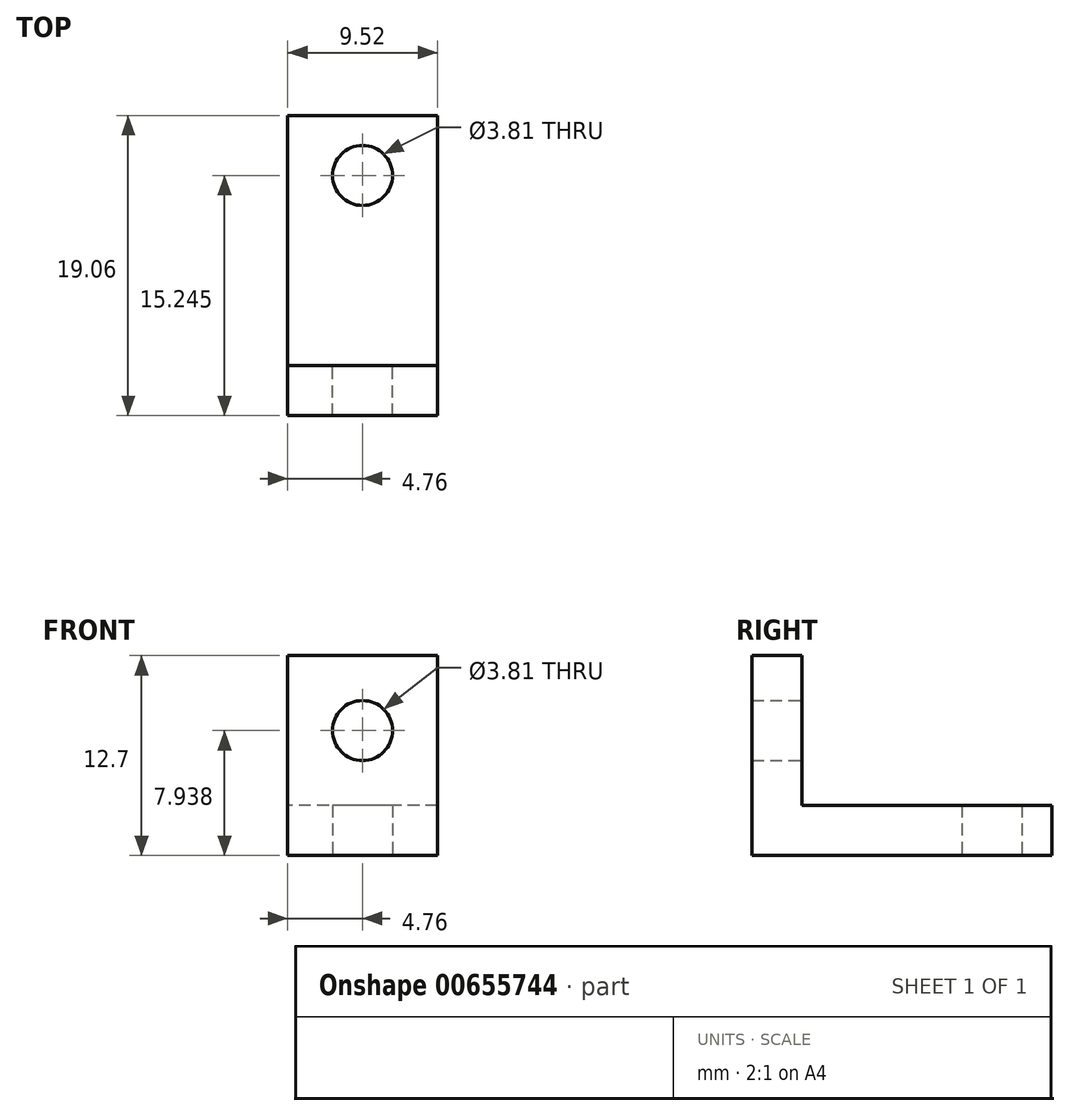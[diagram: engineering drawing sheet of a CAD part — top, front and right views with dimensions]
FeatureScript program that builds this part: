
annotation { "Feature Type Name" : "Feature", "Feature Type Description" : "" }
export const myFeature = defineFeature(function(context is Context, id is Id, definition is map)
    precondition{}
    {
        {
            var Q0;
            Q0=qCreatedBy(makeId("Top.planeOp"),FACE);
            var sketch = newSketch(context, id + "F0", { "sketchPlane" : qUnion([Q0])});
            skLineSegment(sketch, "E0.bottom", {"start": v(4.76, -9.53) * mm, "end": v(-4.76, -9.53) * mm});
            skLineSegment(sketch, "E0.top", {"start": v(4.76, 9.53) * mm, "end": v(-4.76, 9.52) * mm});
            skLineSegment(sketch, "E0.left", {"start": v(4.76, -9.52) * mm, "end": v(4.76, 9.53) * mm});
            skLineSegment(sketch, "E0.right", {"start": v(-4.76, -9.53) * mm, "end": v(-4.76, 9.52) * mm});
            skPoint(sketch, "E0.middle", {"position": v(0, 0) * mm});
            skLineSegment(sketch, "E1", {"start": v(-4.76, -6.35) * mm, "end": v(4.76, -6.35) * mm});
            skCircle(sketch, "E2", {"center": v(0, 5.72) * mm, "radius": 1.9 * mm});
            skPoint(sketch, "E2.centerSnap0", {"position": v(0, 9.53) * mm});
            skSolve(sketch);
        }
        {
            var Q0;
            {var subQ1=sQuery(id+"F0.wireOp",EDGE,"E0.top");Q0=makeQuery(id+"F0.imprint","IMPRINT",FACE,{"disambiguationData":[TD([[makeQuery(id+"F0.imprint","IMPRINT",EDGE,{"derivedFrom":subQ1}),1.0]])]});}
            extrude(context, id + "F1", {"entities" : qUnion([Q0]), "depth" : 3.17 * mm, "offsetDistance" : 25.4 * mm});
        }
        {
            var Q0;
            {var subQ0=sQuery(id+"F0.wireOp",EDGE,"E0.bottom");Q0=makeQuery(id+"F0.imprint","IMPRINT",FACE,{"disambiguationData":[TD([[makeQuery(id+"F0.imprint","IMPRINT",EDGE,{"derivedFrom":subQ0}),-1.0]])]});}
            extrude(context, id + "F2", {"entities" : qUnion([Q0]), "operationType" : NewBodyOperationType.ADD, "depth" : 12.7 * mm, "offsetDistance" : 25.4 * mm});
        }
        {
            var Q0;
            Q0=makeQuery(id+"F2.opExtrude","SWEPT_FACE",FACE,{"disambiguationData":[OSD([sQuery(id+"F0.wireOp",EDGE,"E1")])]});
            var sketch = newSketch(context, id + "F3", { "sketchPlane" : qUnion([Q0])});
            skCircle(sketch, "E3", {"center": v(0, 7.94) * mm, "radius": 1.9 * mm});
            skPoint(sketch, "E3.centerSnap0", {"position": v(4.76, 7.94) * mm});
            skSolve(sketch);
        }
        {
            var Q0;
            Q0=makeQuery(id+"F3.imprint","IMPRINT",FACE,{"disambiguationData":[TD([[makeQuery(id+"F3.imprint","IMPRINT",EDGE,{"derivedFrom":sQuery(id+"F3.wireOp",EDGE,"E3")}),1.0]])]});
            extrude(context, id + "F4", {"entities" : qUnion([Q0]), "operationType" : NewBodyOperationType.REMOVE, "oppositeDirection" : true, "depth" : 25.4 * mm, "offsetDistance" : 25.4 * mm});
        }
    });
